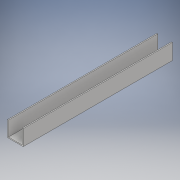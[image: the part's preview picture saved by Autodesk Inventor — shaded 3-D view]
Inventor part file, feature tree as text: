
AUTODESK INVENTOR PART (.ipt)
format: ipt  version: 2017 (Build 210142000, 142)  size: 98,816 bytes
history: native  units: in
note: dims shown in document units (in); Inventor stores cm internally (conversion verified against a paired STEP export)
features: sketch x2, extrude x1
ambient origin geometry x8: Origin, YZ Plane, XZ Plane, XY Plane, X Axis, Y Axis, Z Axis, Center Point
bodies: Solid1 (feature_tree)
feature tree (3):
  sketch  "Sketch1"  dims[d2=0.079in d3=1.26in]
  sketch  "Sketch2"  dims[d5=12.0in d6=0.0in]
  extrude  "Extrusion1"  Depth=1.26in
